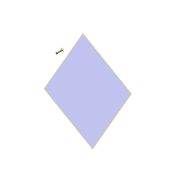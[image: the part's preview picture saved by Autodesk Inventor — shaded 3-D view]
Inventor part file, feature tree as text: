
AUTODESK INVENTOR PART (.ipt)
format: ipt  version: 2016 (Build 200138000, 138)  size: 134,144 bytes
history: native  units: mm
features: sketch x6, extrude x5, plane x2, thread x1, hole x1, chamfer x1
ambient origin geometry x8: Origin, YZ Plane, XZ Plane, XY Plane, X Axis, Y Axis, Z Axis, Center Point
bodies: Solid1 (feature_tree)
feature tree (16):
  plane  "Work Plane1"
  extrude  "Extrusion1"  Depth=36.5mm TaperAngle=0.0deg
  extrude  "Extrusion2"  Depth=4.5mm TaperAngle=0.0deg
  thread  "Thread1"  [1 undecoded]
  plane  "Work Plane2"
  extrude  "Extrusion4"  Depth=1.0mm
  hole  "Hole1"  [1 undecoded]
  extrude  "Extrusion5"  Depth=2.0mm
  extrude  "Extrusion6"  Depth=1.0mm TaperAngle=0.0deg
  chamfer  "Chamfer2"  Distance=0.3mm Angle=45.0deg
  sketch  "Sketch1"  dims[d0=8.0mm d1=36.5mm d2=0.0mm]
  sketch  "Sketch2"  dims[d3=13.0mm d4=4.5mm d5=0.0mm d11=21.0mm d12=0.0mm]
  sketch  "Sketch4"  dims[d16=1.0mm d17=1.0mm]
  sketch  "Sketch5"  dims[d18=0.9mm d19=0.0mm]
  sketch  "Sketch6"  dims[d20=2.459mm d21=10.0mm d22=5.0mm d23=2.0mm d24=90.0deg d25=13.0mm d26=20.594885mm d27=0.2mm d28=0.0mm]
  sketch  "Sketch7"  dims[d29=5.5mm d30=6.8mm d31=1.0mm d32=0.0mm d33=0.3mm d34=2.0mm d35=45.0deg]
note: 2 required parameter values undecoded (feature->parameter linkage not recoverable at this tier; creation-order binding heuristic only, values carry confidence <= 0.55)
